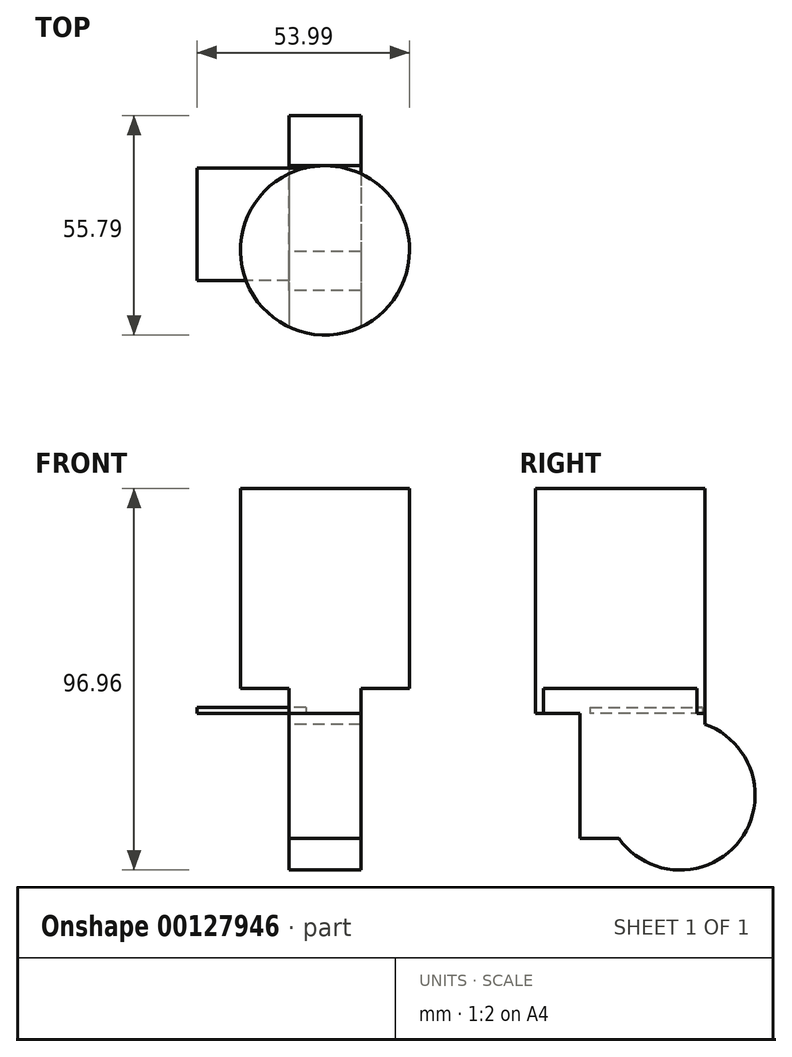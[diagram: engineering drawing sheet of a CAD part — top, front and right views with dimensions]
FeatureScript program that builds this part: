
annotation { "Feature Type Name" : "Feature", "Feature Type Description" : "" }
export const myFeature = defineFeature(function(context is Context, id is Id, definition is map)
    precondition{}
    {
        {
            var Q0;
            Q0=qCreatedBy(makeId("Top.planeOp"),FACE);
            var sketch = newSketch(context, id + "F0", { "sketchPlane" : qUnion([Q0])});
            skCircle(sketch, "E0", {"center": v(0, 0) * mm, "radius": 21.5 * mm});
            skSolve(sketch);
        }
        {
            var Q0;
            Q0=makeQuery(id+"F0.imprint","IMPRINT",FACE,{"disambiguationData":[TD([[makeQuery(id+"F0.imprint","IMPRINT",EDGE,{"derivedFrom":sQuery(id+"F0.wireOp",EDGE,"E0")}),1.0]])]});
            extrude(context, id + "F1", {"entities" : qUnion([Q0]), "depth" : 57.15 * mm});
        }
        {
            var Q0;
            Q0=qCreatedBy(makeId("Front.planeOp"),FACE);
            var sketch = newSketch(context, id + "F2", { "sketchPlane" : qUnion([Q0])});
            skLineSegment(sketch, "E1.bottom", {"start": v(-9.13, 0) * mm, "end": v(9.13, 0) * mm, "construction": true});
            skLineSegment(sketch, "E1.top", {"start": v(-9.12, 6.35) * mm, "end": v(9.12, 6.35) * mm, "construction": true});
            skLineSegment(sketch, "E1.left", {"start": v(-9.12, 6.35) * mm, "end": v(-9.12, 0) * mm});
            skLineSegment(sketch, "E1.right", {"start": v(9.13, 6.35) * mm, "end": v(9.13, 0) * mm});
            skLineSegment(sketch, "E2", {"start": v(-9.12, 6.35) * mm, "end": v(-27.08, 6.35) * mm});
            skLineSegment(sketch, "E3", {"start": v(-27.08, 6.35) * mm, "end": v(-27.08, 0) * mm});
            skLineSegment(sketch, "E4", {"start": v(-27.08, 0) * mm, "end": v(-9.13, 0) * mm});
            skLineSegment(sketch, "E5", {"start": v(9.12, 6.35) * mm, "end": v(26.27, 6.35) * mm});
            skLineSegment(sketch, "E6", {"start": v(26.27, 6.35) * mm, "end": v(26.27, 0) * mm});
            skLineSegment(sketch, "E7", {"start": v(26.27, 0) * mm, "end": v(9.13, 0) * mm});
            skSolve(sketch);
        }
        {
            var Q0;
            Q0 = qSketchRegion(id + "F2", true);
            var Q1;
            Q1=sQuery(id+"F2.wireOp",EDGE,"E1.top");
            var Q2;
            Q2=sQuery(id+"F2.wireOp",EDGE,"E1.bottom");
            extrude(context, id + "F3", {"entities" : qUnion([Q0]), "operationType" : NewBodyOperationType.REMOVE, "surfaceEntities" : qUnion([Q1, Q2]), "endBound" : BoundingType.THROUGH_ALL, "oppositeDirection" : true, "depth" : 25.4 * mm, "hasSecondDirection" : true, "secondDirectionBound" : SecondDirectionBoundingType.THROUGH_ALL, "secondDirectionOppositeDirection" : false, "secondDirectionDepth" : 25.4 * mm});
        }
        {
            var Q0;
            Q0=makeQuery(id+"F3.boolean.opBoolean","COPY",FACE,{"derivedFrom":makeQuery(id+"F3.opExtrude","SWEPT_FACE",FACE,{"disambiguationData":[OSD([sQuery(id+"F2.wireOp",EDGE,"E1.left")])]})});
            var sketch = newSketch(context, id + "F4", { "sketchPlane" : qUnion([Q0])});
            skArc(sketch, "E8", {"start": v(-21.5, -2.77) * mm, "mid": v(-30.46, -32.22) * mm, "end": v(0.32, -31.75) * mm});
            skLineSegment(sketch, "E9", {"start": v(-21.5, 0) * mm, "end": v(-21.5, 57.15) * mm, "construction": true});
            skLineSegment(sketch, "E10", {"start": v(-21.5, 0) * mm, "end": v(-21.5, -2.77) * mm});
            skLineSegment(sketch, "E11", {"start": v(-21.5, 0) * mm, "end": v(10.16, 0) * mm});
            skLineSegment(sketch, "E12", {"start": v(10.16, 0) * mm, "end": v(10.16, -31.75) * mm});
            skLineSegment(sketch, "E13", {"start": v(10.16, -31.75) * mm, "end": v(0.32, -31.75) * mm});
            skSolve(sketch);
        }
        {
            var Q0;
            Q0=makeQuery(id+"F4.imprint","IMPRINT",FACE,{"disambiguationData":[TD([[makeQuery(id+"F4.imprint","IMPRINT",EDGE,{"derivedFrom":sQuery(id+"F4.wireOp",EDGE,"E8")}),1.0]])]});
            var Q1;
            Q1=makeQuery(id+"F3.boolean.opBoolean","COPY",FACE,{"derivedFrom":makeQuery(id+"F3.opExtrude","SWEPT_FACE",FACE,{"disambiguationData":[OSD([sQuery(id+"F2.wireOp",EDGE,"E1.right")])]})});
            extrude(context, id + "F5", {"entities" : qUnion([Q0]), "operationType" : NewBodyOperationType.ADD, "endBound" : BoundingType.UP_TO_SURFACE, "oppositeDirection" : true, "endBoundEntityFace" : qUnion([Q1]), "depth" : 25.4 * mm});
        }
        {
            var Q0;
            Q0=makeQuery(id+"F5.boolean.opBoolean","MERGE",FACE,{"derivedFrom":[makeQuery(id+"F3.boolean.opBoolean","COPY",FACE,{"derivedFrom":makeQuery(id+"F3.opExtrude","SWEPT_FACE",FACE,{"disambiguationData":[OSD([sQuery(id+"F2.wireOp",EDGE,"E1.left")])]})}),makeQuery(id+"F5.opExtrude","CAP_FACE",FACE,{"disambiguationData":[OSD([sQuery(id+"F4.wireOp",EDGE,"E8"),sQuery(id+"F4.wireOp",EDGE,"E10"),sQuery(id+"F4.wireOp",EDGE,"E11"),sQuery(id+"F4.wireOp",EDGE,"E12"),sQuery(id+"F4.wireOp",EDGE,"E13")])],"isStart":true})]});
            var sketch = newSketch(context, id + "F6", { "sketchPlane" : qUnion([Q0])});
            skLineSegment(sketch, "E14.bottom", {"start": v(7.62, 1.52) * mm, "end": v(-20.96, 1.52) * mm});
            skLineSegment(sketch, "E14.top", {"start": v(7.62, 0) * mm, "end": v(-20.96, 0) * mm});
            skLineSegment(sketch, "E14.left", {"start": v(7.62, 1.52) * mm, "end": v(7.62, 0) * mm});
            skLineSegment(sketch, "E14.right", {"start": v(-20.96, 1.52) * mm, "end": v(-20.96, 0) * mm});
            skSolve(sketch);
        }
        {
            var Q0;
            Q0 = qSketchRegion(id + "F6", true);
            extrude(context, id + "F7", {"entities" : qUnion([Q0]), "operationType" : NewBodyOperationType.ADD, "oppositeDirection" : true, "depth" : 6.35 * mm, "hasSecondDirection" : true, "secondDirectionOppositeDirection" : false, "secondDirectionDepth" : 23.37 * mm});
        }
    });
